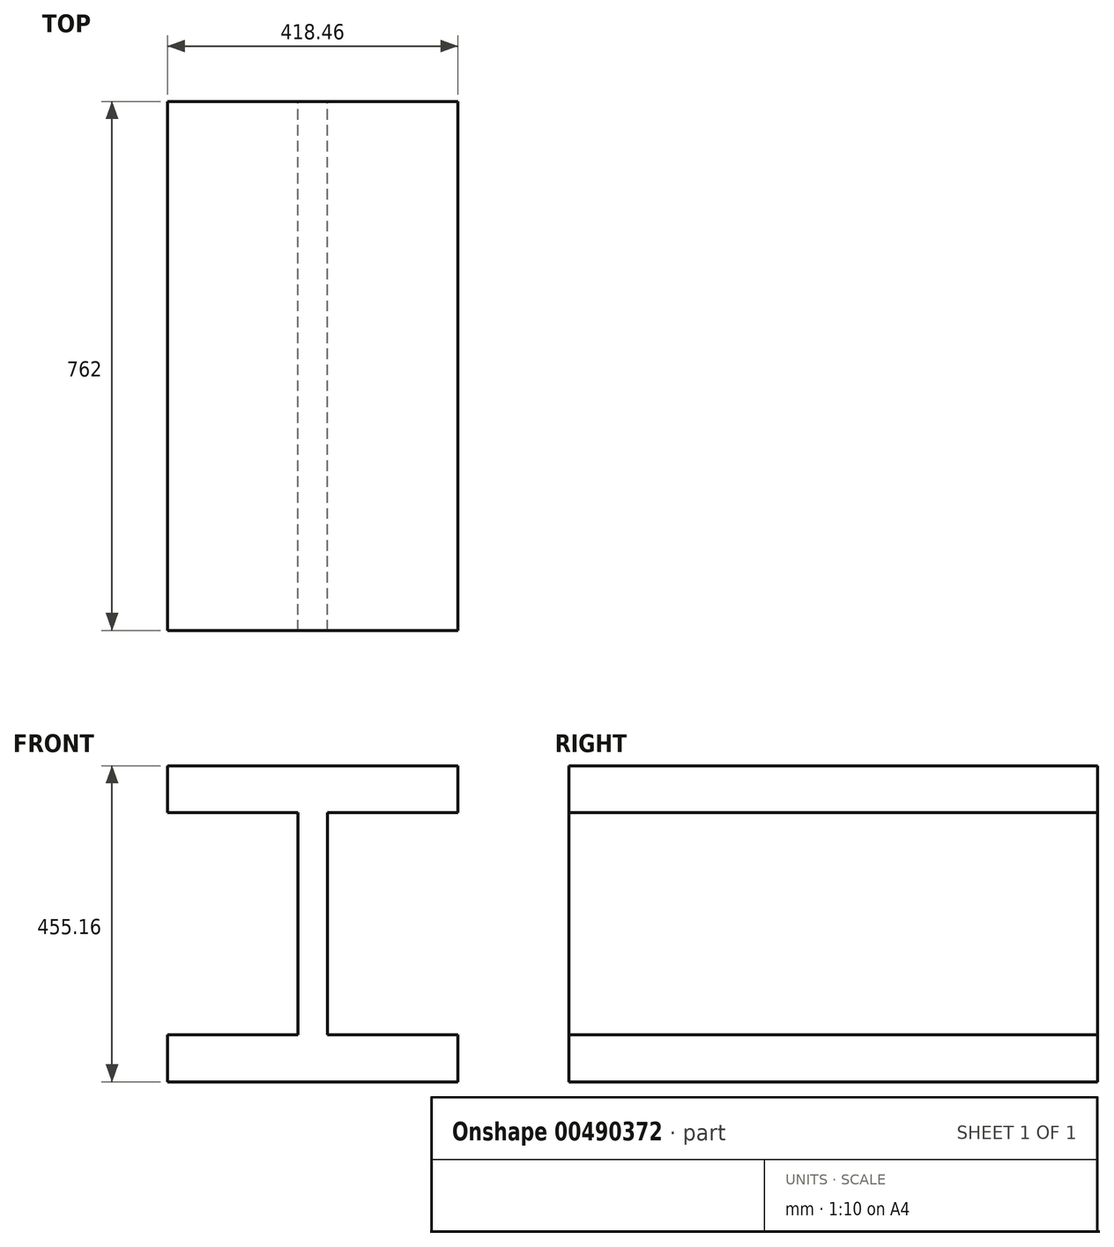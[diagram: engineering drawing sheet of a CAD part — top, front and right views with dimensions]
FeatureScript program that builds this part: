
annotation { "Feature Type Name" : "Feature", "Feature Type Description" : "" }
export const myFeature = defineFeature(function(context is Context, id is Id, definition is map)
    precondition{}
    {
        {
            var Q0;
            Q0=qCreatedBy(makeId("Front.planeOp"),FACE);
            var sketch = newSketch(context, id + "F0", { "sketchPlane" : qUnion([Q0])});
            skLineSegment(sketch, "E0", {"start": v(0, 0) * mm, "end": v(0, 332.47) * mm, "construction": true});
            skLineSegment(sketch, "E1", {"start": v(0, 0) * mm, "end": v(-392.54, 0) * mm, "construction": true});
            skLineSegment(sketch, "E2", {"start": v(0, 0) * mm, "end": v(-21.02, 0) * mm});
            skLineSegment(sketch, "E3", {"start": v(-21.02, 0) * mm, "end": v(-21.02, 160.02) * mm});
            skLineSegment(sketch, "E4", {"start": v(-21.02, 160.02) * mm, "end": v(-209.23, 160.02) * mm});
            skLineSegment(sketch, "E5", {"start": v(-209.23, 160.02) * mm, "end": v(-209.23, 227.58) * mm});
            skLineSegment(sketch, "E6", {"start": v(-209.23, 227.58) * mm, "end": v(0, 227.58) * mm});
            skLineSegment(sketch, "E7", {"start": v(0, 227.58) * mm, "end": v(0, 0) * mm});
            skLineSegment(sketch, "E8.MirrorCS", {"start": v(21.02, 160.02) * mm, "end": v(209.23, 160.02) * mm});
            skLineSegment(sketch, "E9.MirrorCS", {"start": v(209.23, 160.02) * mm, "end": v(209.23, 227.58) * mm});
            skLineSegment(sketch, "E10.MirrorCS", {"start": v(209.23, 227.58) * mm, "end": v(0, 227.58) * mm});
            skLineSegment(sketch, "E11.MirrorCS", {"start": v(21.02, 0) * mm, "end": v(21.02, 160.02) * mm});
            skLineSegment(sketch, "E12.MirrorCS", {"start": v(0, -227.58) * mm, "end": v(0, 0) * mm});
            skLineSegment(sketch, "E13.MirrorCS", {"start": v(21.02, 0) * mm, "end": v(21.02, -160.02) * mm});
            skLineSegment(sketch, "E14.MirrorCS", {"start": v(0, 0) * mm, "end": v(0, -332.47) * mm, "construction": true});
            skLineSegment(sketch, "E15.MirrorCS", {"start": v(-21.02, 0) * mm, "end": v(-21.02, -160.02) * mm});
            skLineSegment(sketch, "E16.MirrorCS", {"start": v(21.02, -160.02) * mm, "end": v(209.23, -160.02) * mm});
            skLineSegment(sketch, "E17.MirrorCS", {"start": v(-209.23, -160.02) * mm, "end": v(-209.23, -227.58) * mm});
            skLineSegment(sketch, "E18.MirrorCS", {"start": v(-21.02, -160.02) * mm, "end": v(-209.23, -160.02) * mm});
            skLineSegment(sketch, "E19.MirrorCS", {"start": v(209.23, -160.02) * mm, "end": v(209.23, -227.58) * mm});
            skLineSegment(sketch, "E20.MirrorCS", {"start": v(209.23, -227.58) * mm, "end": v(0, -227.58) * mm});
            skLineSegment(sketch, "E21.MirrorCS", {"start": v(-209.23, -227.58) * mm, "end": v(0, -227.58) * mm});
            skSolve(sketch);
        }
        {
            var Q0;
            Q0 = qSketchRegion(id + "F0", true);
            extrude(context, id + "F1", {"entities" : qUnion([Q0]), "depth" : 762 * mm});
        }
    });
